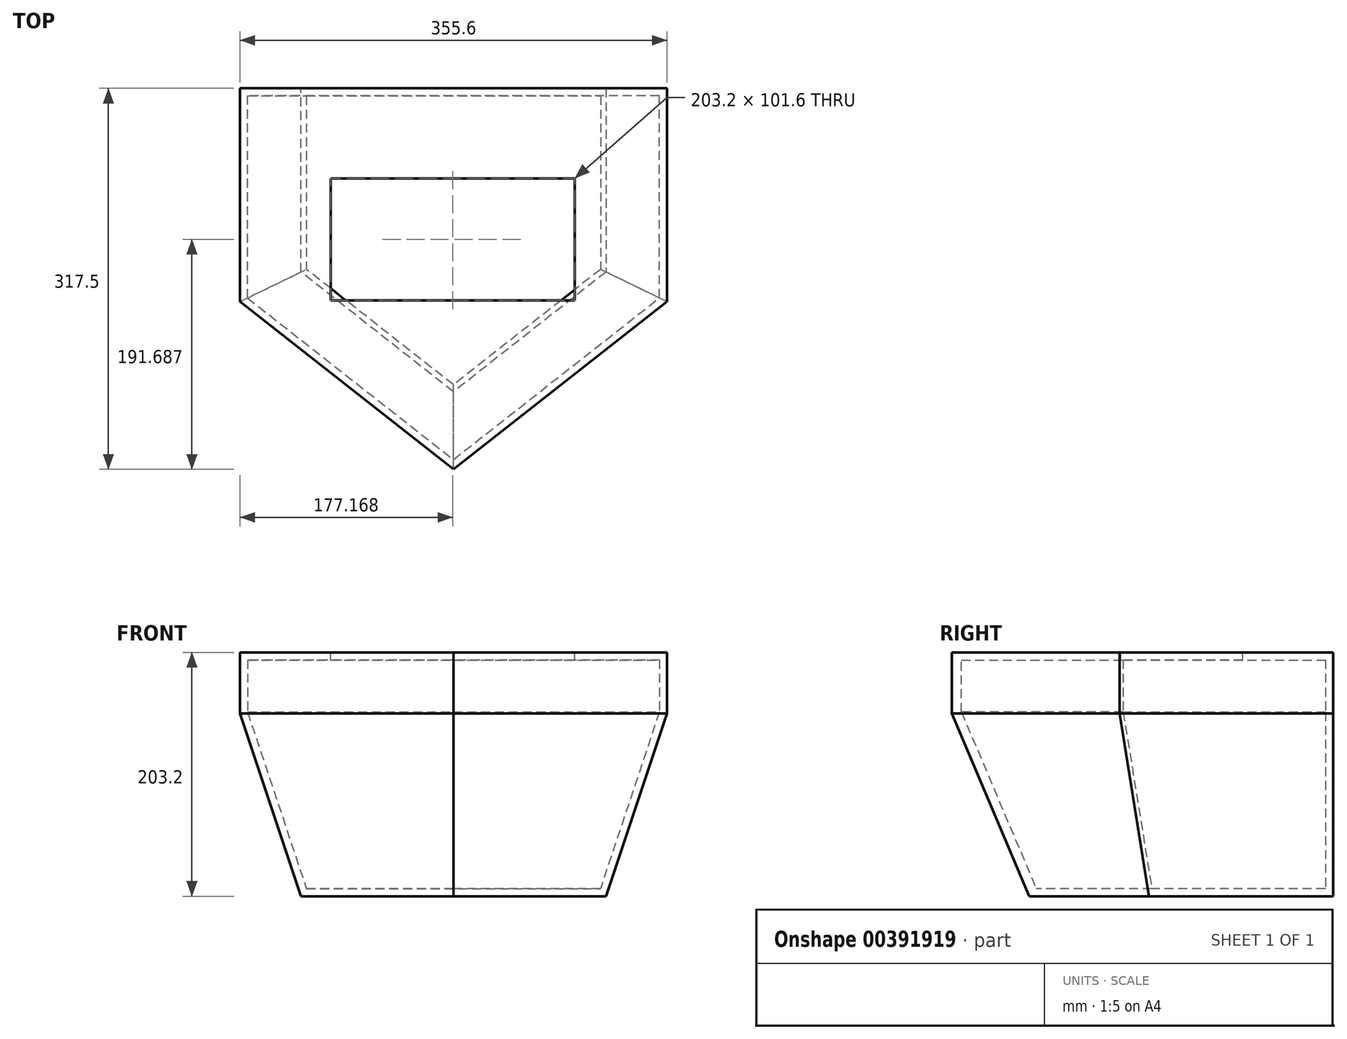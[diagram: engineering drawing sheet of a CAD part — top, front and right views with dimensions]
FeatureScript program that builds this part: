
annotation { "Feature Type Name" : "Feature", "Feature Type Description" : "" }
export const myFeature = defineFeature(function(context is Context, id is Id, definition is map)
    precondition{}
    {
        {
            var Q0;
            Q0=qCreatedBy(makeId("Top.planeOp"),FACE);
            var sketch = newSketch(context, id + "F0", { "sketchPlane" : qUnion([Q0])});
            skLineSegment(sketch, "E0.bottom", {"start": v(-177.8, 88.9) * mm, "end": v(177.8, 88.9) * mm});
            skLineSegment(sketch, "E0.top", {"start": v(-177.8, -88.9) * mm, "end": v(177.8, -88.9) * mm});
            skLineSegment(sketch, "E0.left", {"start": v(-177.8, 88.9) * mm, "end": v(-177.8, -88.9) * mm});
            skLineSegment(sketch, "E0.right", {"start": v(177.8, 88.9) * mm, "end": v(177.8, -88.9) * mm});
            skPoint(sketch, "E0.middle", {"position": v(0, 0) * mm});
            skSolve(sketch);
        }
        {
            var Q0;
            Q0=makeQuery(id+"F0.imprint","IMPRINT",FACE,{"disambiguationData":[TD([[makeQuery(id+"F0.imprint","IMPRINT",EDGE,{"derivedFrom":sQuery(id+"F0.wireOp",EDGE,"E0.bottom")}),-1.0]])]});
            extrude(context, id + "F1", {"entities" : qUnion([Q0]), "depth" : 203.2 * mm});
        }
        {
            var Q0;
            Q0=makeQuery(id+"F1.opExtrude","CAP_EDGE",EDGE,{"disambiguationData":[OSD([sQuery(id+"F0.wireOp",EDGE,"E0.right")])],"isStart":true});
            chamfer(context, id + "F2", {"entities" : qUnion([Q0]), "chamferType" : ChamferType.TWO_OFFSETS, "width1" : 50.8 * mm, "oppositeDirection" : false, "width2" : 152.4 * mm, "tangentPropagation" : true});
        }
        {
            var Q0;
            Q0=makeQuery(id+"F1.opExtrude","CAP_EDGE",EDGE,{"disambiguationData":[OSD([sQuery(id+"F0.wireOp",EDGE,"E0.left")])],"isStart":true});
            chamfer(context, id + "F3", {"entities" : qUnion([Q0]), "chamferType" : ChamferType.TWO_OFFSETS, "width1" : 152.4 * mm, "oppositeDirection" : false, "width2" : 50.8 * mm, "tangentPropagation" : true});
        }
        {
            var Q0;
            Q0=makeQuery(id+"F1.opExtrude","CAP_FACE",FACE,{"disambiguationData":[OSD([sQuery(id+"F0.wireOp",EDGE,"E0.bottom"),sQuery(id+"F0.wireOp",EDGE,"E0.top"),sQuery(id+"F0.wireOp",EDGE,"E0.left"),sQuery(id+"F0.wireOp",EDGE,"E0.right")])],"isStart":true});
            var sketch = newSketch(context, id + "F4", { "sketchPlane" : qUnion([Q0])});
            skLineSegment(sketch, "E1", {"start": v(-127, 88.9) * mm, "end": v(0, 152.41) * mm});
            skPoint(sketch, "E1.endSnap0", {"position": v(0, 88.9) * mm});
            skLineSegment(sketch, "E2", {"start": v(0, 152.41) * mm, "end": v(127, 88.9) * mm});
            skLineSegment(sketch, "E3", {"start": v(127, 88.9) * mm, "end": v(-127, 88.9) * mm});
            skSolve(sketch);
        }
        {
            var Q0;
            Q0=makeQuery(id+"F1.opExtrude","CAP_FACE",FACE,{"disambiguationData":[OSD([sQuery(id+"F0.wireOp",EDGE,"E0.bottom"),sQuery(id+"F0.wireOp",EDGE,"E0.top"),sQuery(id+"F0.wireOp",EDGE,"E0.left"),sQuery(id+"F0.wireOp",EDGE,"E0.right")])],"isStart":false});
            var sketch = newSketch(context, id + "F5", { "sketchPlane" : qUnion([Q0])});
            skLineSegment(sketch, "E4", {"start": v(177.8, -88.9) * mm, "end": v(-177.8, -88.9) * mm});
            skLineSegment(sketch, "E5", {"start": v(-177.8, -88.9) * mm, "end": v(0, -228.6) * mm});
            skLineSegment(sketch, "E6", {"start": v(0, -228.6) * mm, "end": v(177.8, -88.9) * mm});
            skSolve(sketch);
        }
        {
            var Q0;
            Q0=makeQuery(id+"F5.imprint","IMPRINT",FACE,{"disambiguationData":[TD([[makeQuery(id+"F5.imprint","IMPRINT",EDGE,{"derivedFrom":sQuery(id+"F5.wireOp",EDGE,"E4")}),-1.0]])]});
            extrude(context, id + "F6", {"entities" : qUnion([Q0]), "oppositeDirection" : true, "depth" : 50.8 * mm});
        }
        {
            var Q0;
            Q0=makeQuery(id+"F1.opExtrude","SWEPT_BODY",BODY,{"disambiguationData":[OSD([sQuery(id+"F0.wireOp",EDGE,"E0.bottom"),sQuery(id+"F0.wireOp",EDGE,"E0.top"),sQuery(id+"F0.wireOp",EDGE,"E0.left"),sQuery(id+"F0.wireOp",EDGE,"E0.right")])]});
            var Q1;
            Q1=makeQuery(id+"F6.opExtrude","SWEPT_BODY",BODY,{"disambiguationData":[OSD([sQuery(id+"F5.wireOp",EDGE,"E4"),sQuery(id+"F5.wireOp",EDGE,"E5"),sQuery(id+"F5.wireOp",EDGE,"E6")])]});
            booleanBodies(context, id + "F7", {"operationType" : BooleanOperationType.UNION, "tools" : qUnion([Q0, Q1])});
        }
        {
            var Q0;
            Q0=makeQuery(id+"F6.opExtrude","CAP_FACE",FACE,{"disambiguationData":[OSD([sQuery(id+"F5.wireOp",EDGE,"E4"),sQuery(id+"F5.wireOp",EDGE,"E5"),sQuery(id+"F5.wireOp",EDGE,"E6")])],"isStart":false});
            extrude(context, id + "F8", {"entities" : qUnion([Q0]), "operationType" : NewBodyOperationType.ADD, "depth" : 152.4 * mm});
        }
        {
            var Q0;
            Q0=makeQuery(id+"F8.opExtrude","CAP_EDGE",EDGE,{"disambiguationData":[OSD([sQuery(id+"F5.wireOp",EDGE,"E6")])],"isStart":false});
            chamfer(context, id + "F9", {"entities" : qUnion([Q0]), "chamferType" : ChamferType.TWO_OFFSETS, "width1" : 152.4 * mm, "oppositeDirection" : false, "width2" : 50.8 * mm, "tangentPropagation" : true});
        }
        {
            var Q0;
            Q0=makeQuery(id+"F8.opExtrude","CAP_EDGE",EDGE,{"disambiguationData":[OSD([sQuery(id+"F5.wireOp",EDGE,"E5")])],"isStart":false});
            chamfer(context, id + "F10", {"entities" : qUnion([Q0]), "chamferType" : ChamferType.TWO_OFFSETS, "width1" : 152.4 * mm, "oppositeDirection" : false, "width2" : 50.8 * mm, "tangentPropagation" : true});
        }
        {
            var Q0;
            Q0=makeQuery(id+"F7.opBoolean","MERGE",FACE,{"derivedFrom":[makeQuery(id+"F1.opExtrude","CAP_FACE",FACE,{"disambiguationData":[OSD([sQuery(id+"F0.wireOp",EDGE,"E0.bottom"),sQuery(id+"F0.wireOp",EDGE,"E0.top"),sQuery(id+"F0.wireOp",EDGE,"E0.left"),sQuery(id+"F0.wireOp",EDGE,"E0.right")])],"isStart":false}),makeQuery(id+"F6.opExtrude","CAP_FACE",FACE,{"disambiguationData":[OSD([sQuery(id+"F5.wireOp",EDGE,"E4"),sQuery(id+"F5.wireOp",EDGE,"E5"),sQuery(id+"F5.wireOp",EDGE,"E6")])],"isStart":true})]});
            shell(context, id + "F11", {"entities" : qUnion([Q0]), "thickness" : 6.35 * mm});
        }
        {
            var Q0;
            Q0=makeQuery(id+"F6.opExtrude","CAP_VERTEX",VERTEX,{"disambiguationData":[OSD([sQuery(id+"F5.wireOp",EDGE,"E5"),sQuery(id+"F5.wireOp",EDGE,"E6")])],"isStart":true});
            var Q1;
            Q1=makeQuery(id+"F1.opExtrude","CAP_VERTEX",VERTEX,{"disambiguationData":[OSD([sQuery(id+"F0.wireOp",EDGE,"E0.bottom"),sQuery(id+"F0.wireOp",EDGE,"E0.right")])],"isStart":false});
            var Q2;
            Q2=makeQuery(id+"F1.opExtrude","CAP_VERTEX",VERTEX,{"disambiguationData":[OSD([sQuery(id+"F0.wireOp",EDGE,"E0.bottom"),sQuery(id+"F0.wireOp",EDGE,"E0.left")])],"isStart":false});
            cPlane(context, id + "F12", {"entities" : qUnion([Q0, Q1, Q2]), "cplaneType" : CPlaneType.THREE_POINT, "offset" : 203.2 * mm, "oppositeDirection" : true, "width" : 152.4 * mm, "height" : 152.4 * mm});
        }
        {
            var Q0;
            Q0=qCreatedBy(id+"F12.planeOp",FACE);
            var sketch = newSketch(context, id + "F13", { "sketchPlane" : qUnion([Q0])});
            skLineSegment(sketch, "E7", {"start": v(-177.8, 88.9) * mm, "end": v(-177.8, -88.9) * mm});
            skLineSegment(sketch, "E8", {"start": v(-177.8, -88.9) * mm, "end": v(177.8, -88.9) * mm});
            skLineSegment(sketch, "E9", {"start": v(177.8, -88.9) * mm, "end": v(177.8, 88.9) * mm});
            skLineSegment(sketch, "E10", {"start": v(177.8, 88.9) * mm, "end": v(0, 228.6) * mm});
            skLineSegment(sketch, "E11", {"start": v(0, 228.6) * mm, "end": v(-177.8, 88.9) * mm});
            skLineSegment(sketch, "E12.bottom", {"start": v(-102.23, -13.89) * mm, "end": v(100.97, -13.89) * mm});
            skLineSegment(sketch, "E12.top", {"start": v(-102.23, 87.71) * mm, "end": v(100.97, 87.71) * mm});
            skLineSegment(sketch, "E12.left", {"start": v(-102.23, -13.89) * mm, "end": v(-102.23, 87.71) * mm});
            skLineSegment(sketch, "E12.right", {"start": v(100.97, -13.89) * mm, "end": v(100.97, 87.71) * mm});
            skSolve(sketch);
        }
        {
            var Q0;
            Q0=makeQuery(id+"F13.imprint","IMPRINT",FACE,{"disambiguationData":[TD([[makeQuery(id+"F13.imprint","IMPRINT",EDGE,{"derivedFrom":sQuery(id+"F13.wireOp",EDGE,"E7")}),1.0]])]});
            extrude(context, id + "F14", {"entities" : qUnion([Q0]), "operationType" : NewBodyOperationType.ADD, "depth" : 6.35 * mm});
        }
    });
